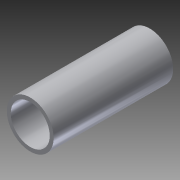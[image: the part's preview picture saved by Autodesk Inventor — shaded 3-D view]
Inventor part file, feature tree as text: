
AUTODESK INVENTOR PART (.ipt)
format: ipt  version: 2014 SP1 (Build 180222100, 222)  size: 83,968 bytes
history: native  units: in
note: dims shown in document units (in); Inventor stores cm internally (conversion verified against a paired STEP export)
features: extrude x1, sketch x1
ambient origin geometry x8: Origin, YZ Plane, XZ Plane, XY Plane, X Axis, Y Axis, Z Axis, Center Point
bodies: Solid1 (feature_tree)
feature tree (2):
  extrude  "Extrusion1"  Depth=1.9147in
  sketch  "Sketch1"  dims[d0=0.75in d1=0.625in d2=1.9147in d3=0.0in]
